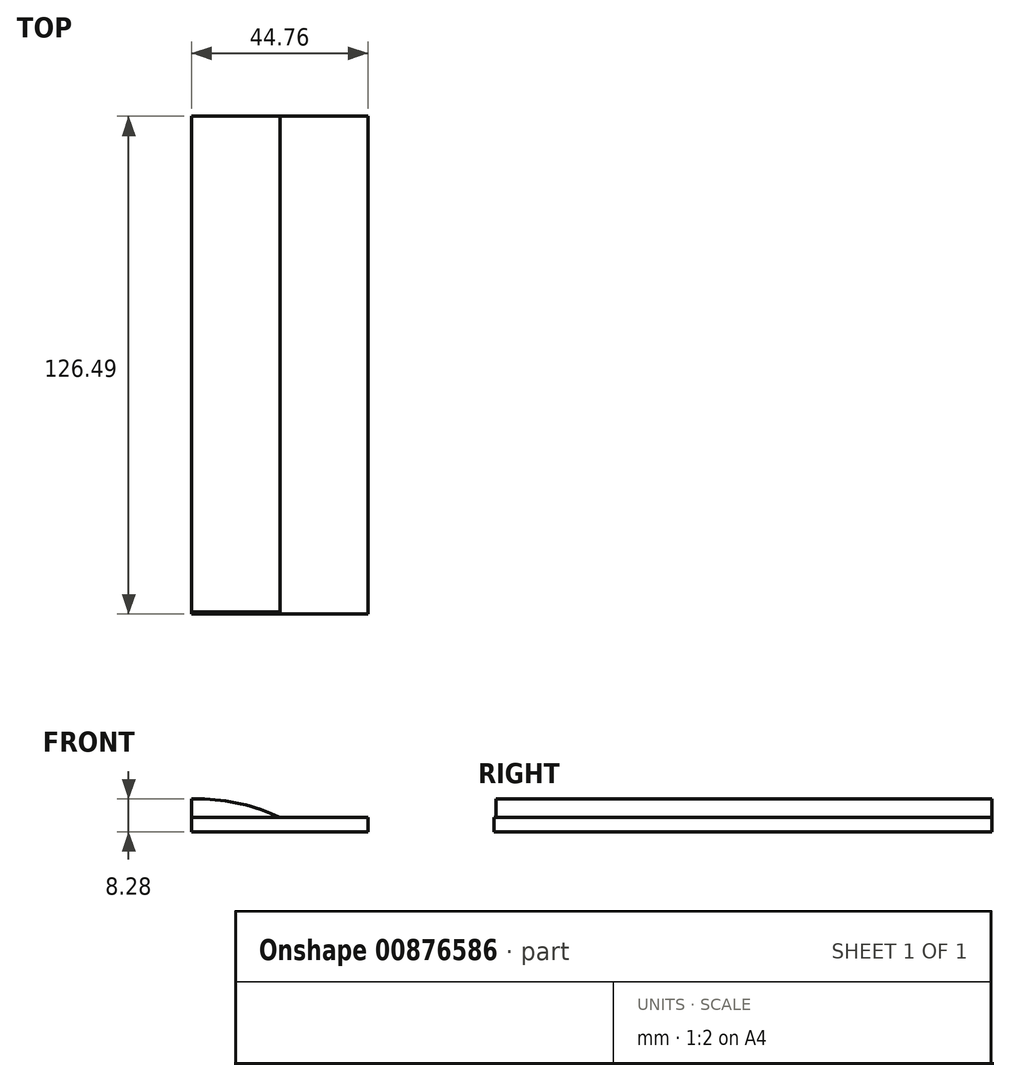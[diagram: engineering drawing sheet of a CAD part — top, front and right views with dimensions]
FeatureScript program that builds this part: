
annotation { "Feature Type Name" : "Feature", "Feature Type Description" : "" }
export const myFeature = defineFeature(function(context is Context, id is Id, definition is map)
    precondition{}
    {
        {
            var Q0;
            Q0=qCreatedBy(makeId("Front.planeOp"),FACE);
            var sketch = newSketch(context, id + "F0", { "sketchPlane" : qUnion([Q0])});
            skLineSegment(sketch, "E0.bottom", {"start": v(0, 0) * mm, "end": v(-22.4, 0) * mm});
            skLineSegment(sketch, "E0.top", {"start": v(0, 4.7) * mm, "end": v(-22.4, 4.7) * mm});
            skLineSegment(sketch, "E0.left", {"start": v(0, 0) * mm, "end": v(0, 4.7) * mm});
            skLineSegment(sketch, "E0.right", {"start": v(-22.4, 0) * mm, "end": v(-22.4, 4.7) * mm});
            skSolve(sketch);
        }
        {
            var Q0;
            Q0=makeQuery(id+"F0.imprint","IMPRINT",FACE,{"disambiguationData":[TD([[makeQuery(id+"F0.imprint","IMPRINT",EDGE,{"derivedFrom":sQuery(id+"F0.wireOp",EDGE,"E0.bottom")}),-1.0]])]});
            extrude(context, id + "F1", {"entities" : qUnion([Q0]), "depth" : 125.98 * mm, "offsetDistance" : 25.4 * mm});
        }
        {
            var Q0;
            Q0=makeQuery(id+"F1.opExtrude","SWEPT_EDGE",EDGE,{"disambiguationData":[OSD([sQuery(id+"F0.wireOp",EDGE,"E0.top"),sQuery(id+"F0.wireOp",EDGE,"E0.left")])]});
            fillet(context, id + "F2", {"entities" : qUnion([Q0]), "radius" : 46.6 * mm, "tangentPropagation" : true, "allowEdgeOverflow" : false});
        }
        {
            var Q0;
            Q0=qCreatedBy(makeId("Front.planeOp"),FACE);
            var sketch = newSketch(context, id + "F3", { "sketchPlane" : qUnion([Q0])});
            skLineSegment(sketch, "E1.bottom", {"start": v(-22.4, 0) * mm, "end": v(22.36, 0) * mm});
            skLineSegment(sketch, "E1.top", {"start": v(-22.4, -3.58) * mm, "end": v(22.36, -3.58) * mm});
            skLineSegment(sketch, "E1.left", {"start": v(-22.4, 0) * mm, "end": v(-22.4, -3.58) * mm});
            skLineSegment(sketch, "E1.right", {"start": v(22.36, 0) * mm, "end": v(22.36, -3.58) * mm});
            skSolve(sketch);
        }
        {
            var Q0;
            Q0 = qSketchRegion(id + "F3", true);
            extrude(context, id + "F4", {"entities" : qUnion([Q0]), "operationType" : NewBodyOperationType.ADD, "depth" : 126.5 * mm, "offsetDistance" : 25.4 * mm});
        }
    });
